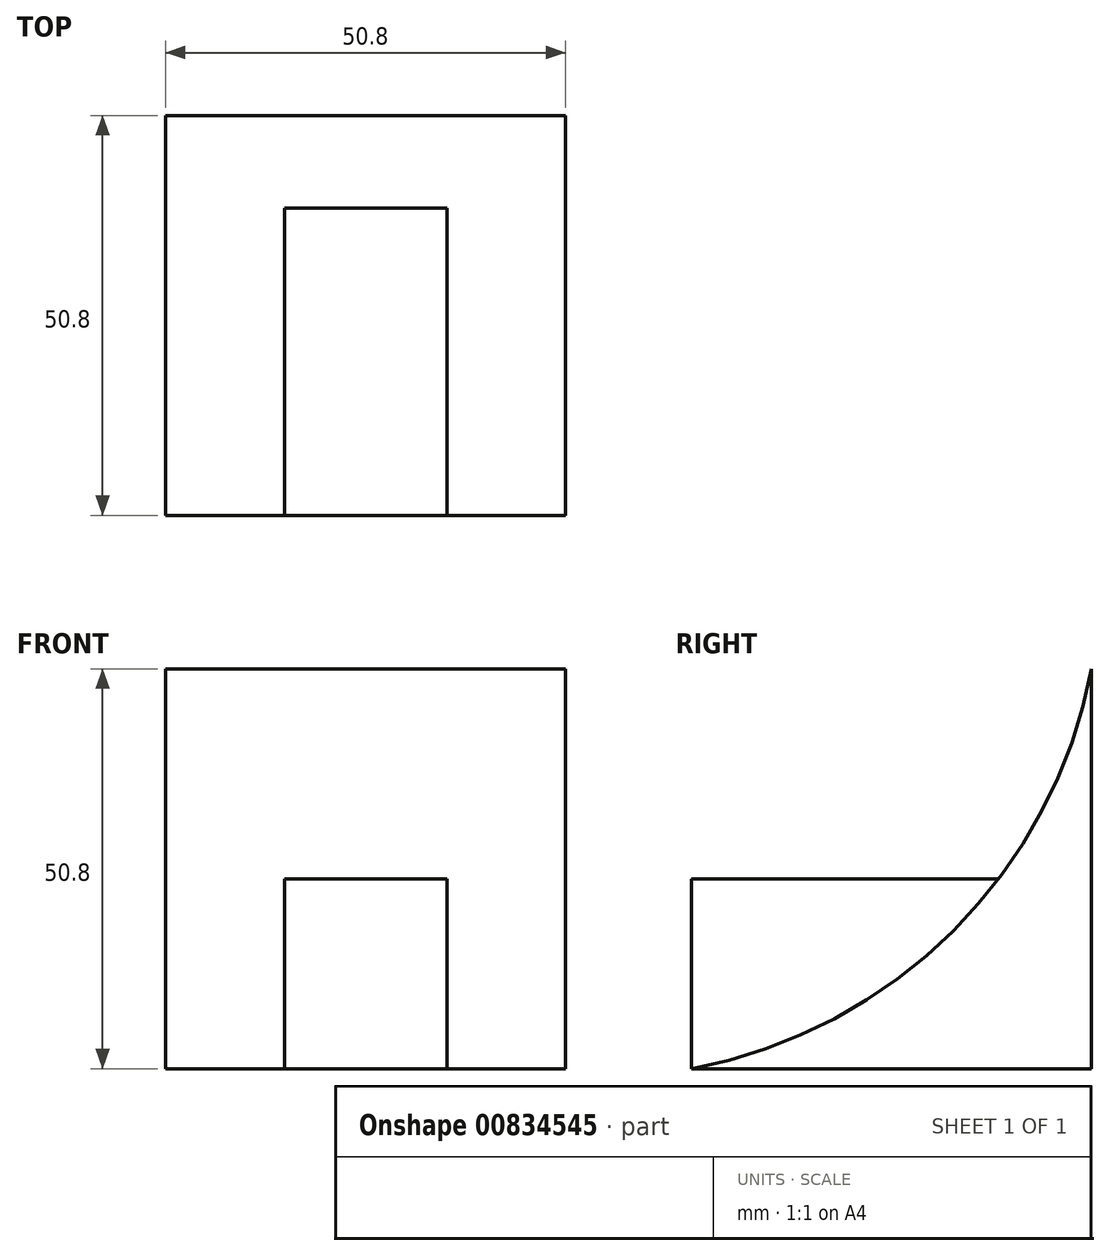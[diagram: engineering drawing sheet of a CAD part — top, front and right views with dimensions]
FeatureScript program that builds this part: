
annotation { "Feature Type Name" : "Feature", "Feature Type Description" : "" }
export const myFeature = defineFeature(function(context is Context, id is Id, definition is map)
    precondition{}
    {
        {
            var Q0;
            Q0=qCreatedBy(makeId("Right.planeOp"),FACE);
            var sketch = newSketch(context, id + "F0", { "sketchPlane" : qUnion([Q0])});
            skLineSegment(sketch, "E0", {"start": v(0, 0) * mm, "end": v(0, 50.8) * mm});
            skLineSegment(sketch, "E1", {"start": v(0, 0) * mm, "end": v(-50.8, 0) * mm});
            skArc(sketch, "E2", {"start": v(-50.8, 0) * mm, "mid": v(-17.53, 17.53) * mm, "end": v(0, 50.8) * mm});
            skLineSegment(sketch, "E3.bottom", {"start": v(0, 24.13) * mm, "end": v(-50.8, 24.13) * mm});
            skLineSegment(sketch, "E3.left", {"start": v(0, 24.13) * mm, "end": v(0, 0) * mm});
            skLineSegment(sketch, "E3.right", {"start": v(-50.8, 24.13) * mm, "end": v(-50.8, 0) * mm});
            skSolve(sketch);
        }
        {
            var Q0;
            {var subQ3=sQuery(id+"F0.wireOp",EDGE,"E1");Q0=makeQuery(id+"F0.imprint","IMPRINT",FACE,{"disambiguationData":[TD([[makeQuery(id+"F0.imprint","IMPRINT",EDGE,{"derivedFrom":subQ3}),-1.0]])]});}
            var Q1;
            {var subQ0=sQuery(id+"F0.wireOp",EDGE,"E3.bottom");var subQ1=sQuery(id+"F0.wireOp",EDGE,"E0");var subQ2=makeQuery(id+"F0.imprint","INTERSECT",VERTEX,{"derivedFrom":[subQ1,subQ0]});Q1=makeQuery(id+"F0.imprint","IMPRINT",FACE,{"disambiguationData":[TD([[makeQuery(id+"F0.imprint","IMPRINT",EDGE,{"disambiguationData":[TD([[subQ2,-1.0]])],"derivedFrom":subQ1}),1.0]])]});}
            extrude(context, id + "F1", {"entities" : qUnion([Q0, Q1]), "depth" : 50.8 * mm, "offsetDistance" : 25.4 * mm});
        }
        {
            var Q0;
            {var subQ0=sQuery(id+"F0.wireOp",EDGE,"E3.bottom");var subQ1=sQuery(id+"F0.wireOp",EDGE,"E0");var subQ2=makeQuery(id+"F0.imprint","INTERSECT",VERTEX,{"derivedFrom":[subQ1,subQ0]});var subQ3=sQuery(id+"F0.wireOp",EDGE,"E1");var subQ7=sQuery(id+"F0.wireOp",EDGE,"E3.right");Q0=qUnion([makeQuery(id+"F0.imprint","IMPRINT",FACE,{"disambiguationData":[TD([[makeQuery(id+"F0.imprint","IMPRINT",EDGE,{"disambiguationData":[TD([[subQ2,-1.0]])],"derivedFrom":subQ1}),1.0]])]}),makeQuery(id+"F0.imprint","IMPRINT",FACE,{"disambiguationData":[TD([[makeQuery(id+"F0.imprint","IMPRINT",EDGE,{"derivedFrom":subQ7}),1.0]])]}),makeQuery(id+"F0.imprint","IMPRINT",FACE,{"disambiguationData":[TD([[makeQuery(id+"F0.imprint","IMPRINT",EDGE,{"derivedFrom":subQ3}),-1.0]])]})]);}
            extrude(context, id + "F2", {"entities" : qUnion([Q0]), "operationType" : NewBodyOperationType.ADD, "depth" : 35.72 * mm, "offsetDistance" : 25.4 * mm});
        }
        {
            var Q0;
            {var subQ0=sQuery(id+"F0.wireOp",EDGE,"E3.right");Q0=makeQuery(id+"F0.imprint","IMPRINT",FACE,{"disambiguationData":[TD([[makeQuery(id+"F0.imprint","IMPRINT",EDGE,{"derivedFrom":subQ0}),1.0]])]});}
            extrude(context, id + "F3", {"entities" : qUnion([Q0]), "operationType" : NewBodyOperationType.REMOVE, "depth" : 15.08 * mm, "offsetDistance" : 25.4 * mm});
        }
    });
